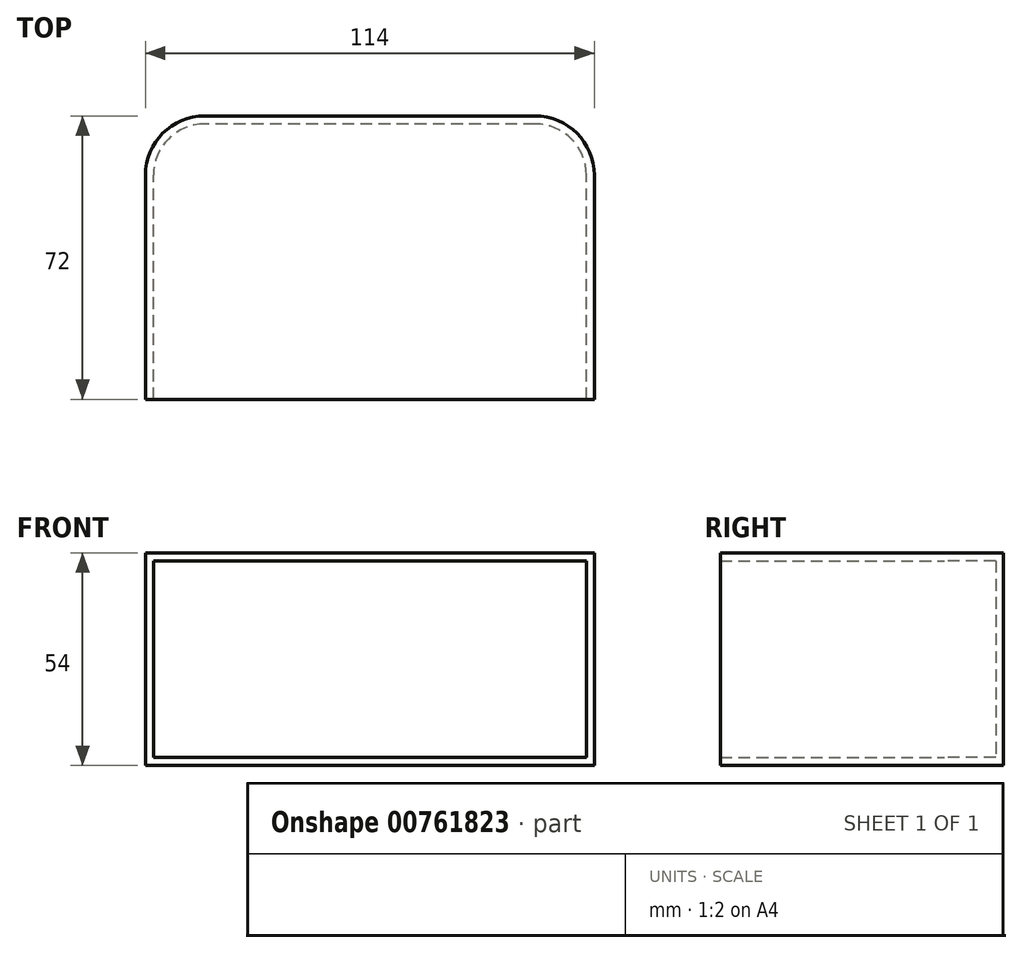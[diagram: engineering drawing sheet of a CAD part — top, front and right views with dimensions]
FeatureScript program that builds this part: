
annotation { "Feature Type Name" : "Feature", "Feature Type Description" : "" }
export const myFeature = defineFeature(function(context is Context, id is Id, definition is map)
    precondition{}
    {
        {
            var Q0;
            Q0=qCreatedBy(makeId("Top.planeOp"),FACE);
            var sketch = newSketch(context, id + "F0", { "sketchPlane" : qUnion([Q0])});
            skLineSegment(sketch, "E0", {"start": v(0, 0) * mm, "end": v(0, 72) * mm, "construction": true});
            skLineSegment(sketch, "E1.MirrorCS", {"start": v(-57, 0) * mm, "end": v(-57, 57) * mm});
            skLineSegment(sketch, "E2.MirrorCS", {"start": v(0, 0) * mm, "end": v(-57, 0) * mm});
            skLineSegment(sketch, "E3", {"start": v(-42, 72) * mm, "end": v(-42, 72) * mm});
            skPoint(sketch, "E4.visualSharp", {"position": v(-57, 72) * mm});
            skArc(sketch, "E4.filletArc", {"start": v(-42, 72) * mm, "mid": v(-52.6, 67.6) * mm, "end": v(-57, 57) * mm});
            skLineSegment(sketch, "E5", {"start": v(0, 72) * mm, "end": v(-42, 72) * mm});
            skLineSegment(sketch, "E6.MirrorCS", {"start": v(57, 0) * mm, "end": v(57, 57) * mm});
            skLineSegment(sketch, "E7.MirrorCS", {"start": v(0, 72) * mm, "end": v(42, 72) * mm});
            skArc(sketch, "E8.MirrorCS", {"start": v(42, 72) * mm, "mid": v(52.6, 67.6) * mm, "end": v(57, 57) * mm});
            skLineSegment(sketch, "E9.MirrorCS", {"start": v(57, 57) * mm, "end": v(57, 57) * mm});
            skLineSegment(sketch, "E10.MirrorCS", {"start": v(0, 0) * mm, "end": v(57, 0) * mm});
            skPoint(sketch, "E11.MirrorP", {"position": v(57, 72) * mm});
            skSolve(sketch);
        }
        {
            var Q0;
            Q0 = qSketchRegion(id + "F0", true);
            extrude(context, id + "F1", {"entities" : qUnion([Q0]), "depth" : 54 * mm, "offsetDistance" : 25 * mm});
        }
        {
            var Q0;
            Q0=makeQuery(id+"F1.opExtrude","SWEPT_FACE",FACE,{"disambiguationData":[OSD([sQuery(id+"F0.wireOp",EDGE,"E2.MirrorCS"),sQuery(id+"F0.wireOp",EDGE,"E10.MirrorCS")])]});
            shell(context, id + "F2", {"entities" : qUnion([Q0]), "thickness" : 2 * mm});
        }
    });
